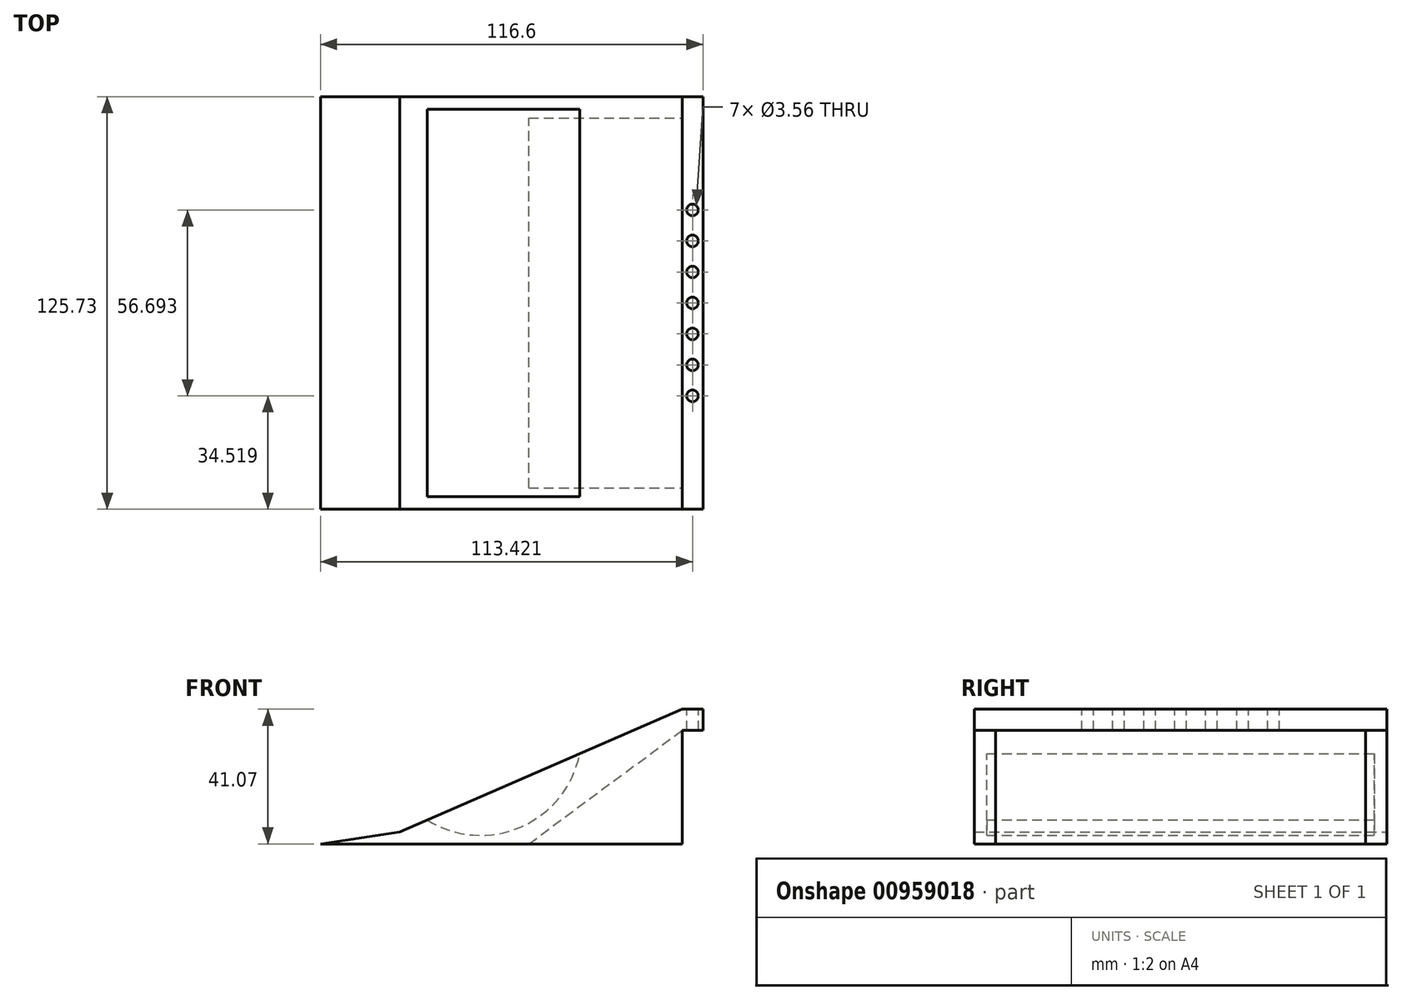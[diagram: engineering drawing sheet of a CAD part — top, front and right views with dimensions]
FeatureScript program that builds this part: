
annotation { "Feature Type Name" : "Feature", "Feature Type Description" : "" }
export const myFeature = defineFeature(function(context is Context, id is Id, definition is map)
    precondition{}
    {
        {
            var Q0;
            Q0=qCreatedBy(makeId("Front.planeOp"),FACE);
            var sketch = newSketch(context, id + "F0", { "sketchPlane" : qUnion([Q0])});
            skLineSegment(sketch, "E0.top", {"start": v(23.37, -17.3) * mm, "end": v(-23.37, -17.3) * mm, "construction": true});
            skLineSegment(sketch, "E0.left", {"start": v(23.37, 17.3) * mm, "end": v(23.37, -17.3) * mm, "construction": true});
            skPoint(sketch, "E0.middle", {"position": v(0, 0) * mm});
            skLineSegment(sketch, "E1", {"start": v(-23.37, -17.3) * mm, "end": v(23.37, 17.3) * mm});
            skLineSegment(sketch, "E2", {"start": v(-23.37, -17.3) * mm, "end": v(-71, -17.3) * mm});
            skLineSegment(sketch, "E3.bottom", {"start": v(23.37, 17.3) * mm, "end": v(29.72, 17.3) * mm});
            skLineSegment(sketch, "E3.top", {"start": v(23.37, 23.77) * mm, "end": v(29.72, 23.77) * mm});
            skLineSegment(sketch, "E3.left", {"start": v(23.37, 17.3) * mm, "end": v(23.37, 23.77) * mm});
            skLineSegment(sketch, "E3.right", {"start": v(29.72, 17.3) * mm, "end": v(29.72, 23.77) * mm});
            skLineSegment(sketch, "E4", {"start": v(23.37, 23.77) * mm, "end": v(-7.83, 10.2) * mm});
            skLineSegment(sketch, "E5.trimOffspring", {"start": v(-54.32, -10.04) * mm, "end": v(-62.66, -13.67) * mm});
            skArc(sketch, "E6", {"start": v(-54.32, -10.04) * mm, "mid": v(-25.76, -12.13) * mm, "end": v(-7.83, 10.2) * mm});
            skLineSegment(sketch, "E7", {"start": v(-71, -17.3) * mm, "end": v(-86.88, -17.3) * mm});
            skLineSegment(sketch, "E8", {"start": v(-62.66, -13.67) * mm, "end": v(-86.88, -17.3) * mm});
            skPoint(sketch, "E9.orphan", {"position": v(-102.75, -17.3) * mm});
            skSolve(sketch);
        }
        {
            var Q0;
            Q0=makeQuery(id+"F0.imprint","IMPRINT",FACE,{"disambiguationData":[TD([[makeQuery(id+"F0.imprint","IMPRINT",EDGE,{"derivedFrom":sQuery(id+"F0.wireOp",EDGE,"E1")}),1.0]])]});
            var Q1;
            Q1=makeQuery(id+"F0.imprint","IMPRINT",FACE,{"disambiguationData":[TD([[makeQuery(id+"F0.imprint","IMPRINT",EDGE,{"derivedFrom":sQuery(id+"F0.wireOp",EDGE,"E3.bottom")}),1.0]])]});
            extrude(context, id + "F1", {"entities" : qUnion([Q0, Q1]), "depth" : 118.11 * mm, "offsetDistance" : 25.4 * mm});
        }
        {
            var Q0;
            Q0=makeQuery(id+"F1.opExtrude","SWEPT_FACE",FACE,{"disambiguationData":[OSD([sQuery(id+"F0.wireOp",EDGE,"E3.top")])]});
            var sketch = newSketch(context, id + "F2", { "sketchPlane" : qUnion([Q0])});
            skLineSegment(sketch, "E10", {"start": v(26.54, 0) * mm, "end": v(26.54, -118.11) * mm, "construction": true});
            skCircle(sketch, "E11", {"center": v(26.54, -59.06) * mm, "radius": 1.78 * mm});
            skCircle(sketch, "E12", {"center": v(26.54, -49.6) * mm, "radius": 1.78 * mm});
            skCircle(sketch, "E13", {"center": v(26.54, -40.16) * mm, "radius": 1.78 * mm});
            skCircle(sketch, "E14", {"center": v(26.54, -68.5) * mm, "radius": 1.78 * mm});
            skCircle(sketch, "E15", {"center": v(26.54, -77.95) * mm, "radius": 1.78 * mm});
            skCircle(sketch, "E16", {"center": v(26.54, -30.7) * mm, "radius": 1.78 * mm});
            skCircle(sketch, "E17", {"center": v(26.54, -87.4) * mm, "radius": 1.78 * mm});
            skSolve(sketch);
        }
        {
            var Q0;
            Q0 = qSketchRegion(id + "F2", true);
            extrude(context, id + "F3", {"entities" : qUnion([Q0]), "operationType" : NewBodyOperationType.REMOVE, "oppositeDirection" : true, "depth" : 25.4 * mm, "offsetDistance" : 25.4 * mm});
        }
        {
            var Q0;
            Q0=makeQuery(id+"F1.opExtrude","SWEPT_FACE",FACE,{"disambiguationData":[OSD([sQuery(id+"F0.wireOp",EDGE,"E2")])]});
            var sketch = newSketch(context, id + "F4", { "sketchPlane" : qUnion([Q0])});
            skLineSegment(sketch, "E18.bottom", {"start": v(-23.37, 118.11) * mm, "end": v(23.36, 118.11) * mm});
            skLineSegment(sketch, "E18.top", {"start": v(-23.37, 115.44) * mm, "end": v(23.36, 115.44) * mm});
            skLineSegment(sketch, "E18.left", {"start": v(-23.37, 118.11) * mm, "end": v(-23.37, 115.44) * mm});
            skLineSegment(sketch, "E18.right", {"start": v(23.36, 118.11) * mm, "end": v(23.36, 115.44) * mm});
            skLineSegment(sketch, "E19.MirrorCS", {"start": v(23.36, 0) * mm, "end": v(23.36, 2.67) * mm});
            skLineSegment(sketch, "E20.MirrorCS", {"start": v(-23.37, 0) * mm, "end": v(23.36, 0) * mm});
            skLineSegment(sketch, "E21.MirrorCS", {"start": v(-23.37, 0) * mm, "end": v(-23.37, 2.67) * mm});
            skLineSegment(sketch, "E22.MirrorCS", {"start": v(-23.37, 2.67) * mm, "end": v(23.36, 2.67) * mm});
            skSolve(sketch);
        }
        {
            var Q0;
            Q0 = qSketchRegion(id + "F4", true);
            var Q1;
            Q1=makeQuery(id+"F1.opExtrude","SWEPT_FACE",FACE,{"disambiguationData":[OSD([sQuery(id+"F0.wireOp",EDGE,"E1")])]});
            extrude(context, id + "F5", {"entities" : qUnion([Q0]), "operationType" : NewBodyOperationType.ADD, "endBound" : BoundingType.UP_TO_SURFACE, "oppositeDirection" : true, "depth" : 25.4 * mm, "endBoundEntityFace" : qUnion([Q1]), "offsetDistance" : 25.4 * mm});
        }
        {
            var Q0;
            Q0=makeQuery(id+"F5.boolean.opBoolean","MERGE",FACE,{"derivedFrom":[makeQuery(id+"F1.opExtrude","CAP_FACE",FACE,{"disambiguationData":[OSD([sQuery(id+"F0.wireOp",EDGE,"E1"),sQuery(id+"F0.wireOp",EDGE,"E2"),sQuery(id+"F0.wireOp",EDGE,"E3.bottom"),sQuery(id+"F0.wireOp",EDGE,"E3.top"),sQuery(id+"F0.wireOp",EDGE,"E3.right"),sQuery(id+"F0.wireOp",EDGE,"E4"),sQuery(id+"F0.wireOp",EDGE,"E5.trimOffspring"),sQuery(id+"F0.wireOp",EDGE,"E6")])],"isStart":false}),makeQuery(id+"F5.opExtrude","SWEPT_FACE",FACE,{"disambiguationData":[OSD([sQuery(id+"F4.wireOp",EDGE,"E18.bottom")])]})]});
            extrude(context, id + "F6", {"entities" : qUnion([Q0]), "operationType" : NewBodyOperationType.ADD, "depth" : 3.8 * mm, "offsetDistance" : 25.4 * mm});
        }
        {
            var Q0;
            Q0=makeQuery(id+"F6.opExtrude","CAP_FACE",FACE,{"disambiguationData":[OSD([sQuery(id+"F0.wireOp",EDGE,"E1"),sQuery(id+"F0.wireOp",EDGE,"E2"),sQuery(id+"F0.wireOp",EDGE,"E3.bottom"),sQuery(id+"F0.wireOp",EDGE,"E3.top"),sQuery(id+"F0.wireOp",EDGE,"E3.right"),sQuery(id+"F0.wireOp",EDGE,"E4"),sQuery(id+"F0.wireOp",EDGE,"E5.trimOffspring"),sQuery(id+"F0.wireOp",EDGE,"E6"),sQuery(id+"F4.wireOp",EDGE,"E18.bottom")])],"isStart":false});
            var sketch = newSketch(context, id + "F7", { "sketchPlane" : qUnion([Q0])});
            skArc(sketch, "E23", {"start": v(-54.32, -10.04) * mm, "mid": v(-25.76, -12.13) * mm, "end": v(-7.83, 10.2) * mm});
            skLineSegment(sketch, "E24", {"start": v(-54.32, -10.04) * mm, "end": v(-7.83, 10.2) * mm});
            skSolve(sketch);
        }
        {
            var Q0;
            Q0 = qSketchRegion(id + "F7", true);
            extrude(context, id + "F8", {"entities" : qUnion([Q0]), "operationType" : NewBodyOperationType.ADD, "oppositeDirection" : true, "depth" : 3.8 * mm, "offsetDistance" : 25.4 * mm});
        }
        {
            var Q0;
            Q0=makeQuery(id+"F5.boolean.opBoolean","MERGE",FACE,{"derivedFrom":[makeQuery(id+"F1.opExtrude","CAP_FACE",FACE,{"disambiguationData":[OSD([sQuery(id+"F0.wireOp",EDGE,"E1"),sQuery(id+"F0.wireOp",EDGE,"E2"),sQuery(id+"F0.wireOp",EDGE,"E3.bottom"),sQuery(id+"F0.wireOp",EDGE,"E3.top"),sQuery(id+"F0.wireOp",EDGE,"E3.right"),sQuery(id+"F0.wireOp",EDGE,"E4"),sQuery(id+"F0.wireOp",EDGE,"E5.trimOffspring"),sQuery(id+"F0.wireOp",EDGE,"E6")])],"isStart":true}),makeQuery(id+"F5.opExtrude","SWEPT_FACE",FACE,{"disambiguationData":[OSD([sQuery(id+"F4.wireOp",EDGE,"E20.MirrorCS")])]})]});
            extrude(context, id + "F9", {"entities" : qUnion([Q0]), "operationType" : NewBodyOperationType.ADD, "depth" : 3.8 * mm, "offsetDistance" : 25.4 * mm});
        }
        {
            var Q0;
            Q0=makeQuery(id+"F9.opExtrude","CAP_FACE",FACE,{"disambiguationData":[OSD([sQuery(id+"F0.wireOp",EDGE,"E1"),sQuery(id+"F0.wireOp",EDGE,"E2"),sQuery(id+"F0.wireOp",EDGE,"E3.bottom"),sQuery(id+"F0.wireOp",EDGE,"E3.top"),sQuery(id+"F0.wireOp",EDGE,"E3.right"),sQuery(id+"F0.wireOp",EDGE,"E4"),sQuery(id+"F0.wireOp",EDGE,"E5.trimOffspring"),sQuery(id+"F0.wireOp",EDGE,"E6"),sQuery(id+"F4.wireOp",EDGE,"E20.MirrorCS")])],"isStart":false});
            var sketch = newSketch(context, id + "F10", { "sketchPlane" : qUnion([Q0])});
            skArc(sketch, "E25", {"start": v(7.83, 10.2) * mm, "mid": v(25.76, -12.13) * mm, "end": v(54.32, -10.04) * mm});
            skLineSegment(sketch, "E26", {"start": v(7.83, 10.2) * mm, "end": v(54.32, -10.04) * mm});
            skSolve(sketch);
        }
        {
            var Q0;
            Q0 = qSketchRegion(id + "F10", true);
            extrude(context, id + "F11", {"entities" : qUnion([Q0]), "operationType" : NewBodyOperationType.ADD, "oppositeDirection" : true, "depth" : 3.8 * mm, "offsetDistance" : 25.4 * mm});
        }
    });
